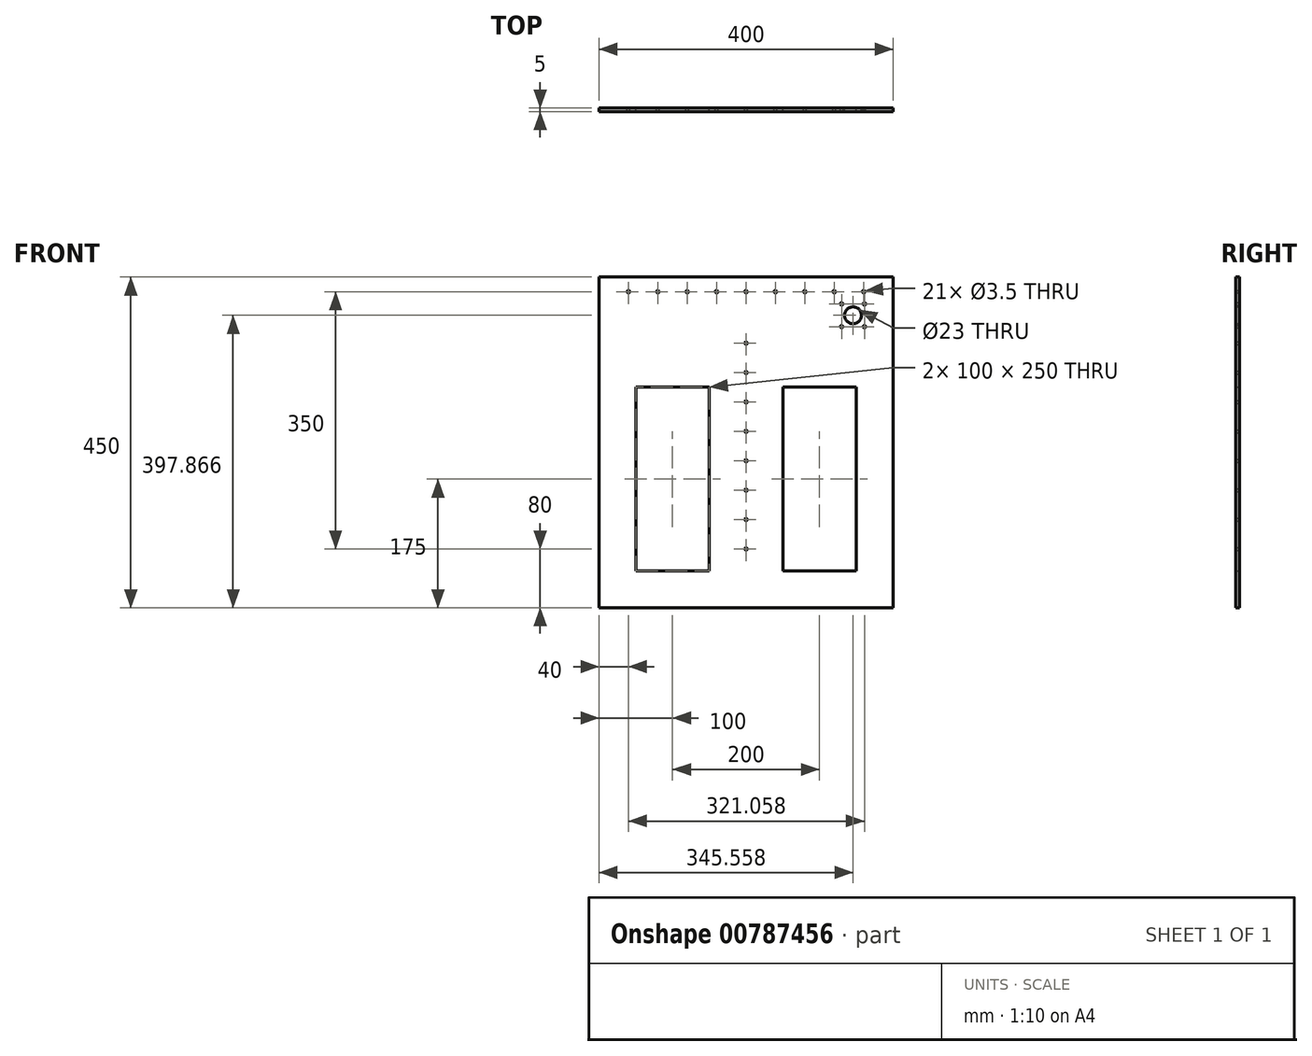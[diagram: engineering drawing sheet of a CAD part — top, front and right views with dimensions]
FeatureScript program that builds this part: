
annotation { "Feature Type Name" : "Feature", "Feature Type Description" : "" }
export const myFeature = defineFeature(function(context is Context, id is Id, definition is map)
    precondition{}
    {
        {
            var Q0;
            Q0=qCreatedBy(makeId("Front.planeOp"),FACE);
            var sketch = newSketch(context, id + "F0", { "sketchPlane" : qUnion([Q0])});
            skLineSegment(sketch, "E0.bottom", {"start": v(0, 0) * mm, "end": v(400, 0) * mm});
            skLineSegment(sketch, "E0.top", {"start": v(0, 450) * mm, "end": v(400, 450) * mm});
            skLineSegment(sketch, "E0.left", {"start": v(0, 0) * mm, "end": v(0, 450) * mm});
            skLineSegment(sketch, "E0.right", {"start": v(400, 0) * mm, "end": v(400, 450) * mm});
            skLineSegment(sketch, "E1", {"start": v(200, 0) * mm, "end": v(200, 450) * mm, "construction": true});
            skLineSegment(sketch, "E2", {"start": v(20.39, 430) * mm, "end": v(471, 430) * mm, "construction": true});
            skCircle(sketch, "E3", {"center": v(40, 430) * mm, "radius": 1.75 * mm});
            skCircle(sketch, "E4.1.0.0", {"center": v(80, 430) * mm, "radius": 1.75 * mm});
            skCircle(sketch, "E4.2.0.0", {"center": v(120, 430) * mm, "radius": 1.75 * mm});
            skCircle(sketch, "E4.3.0.0", {"center": v(160, 430) * mm, "radius": 1.75 * mm});
            skCircle(sketch, "E4.4.0.0", {"center": v(200, 430) * mm, "radius": 1.75 * mm});
            skCircle(sketch, "E4.5.0.0", {"center": v(240, 430) * mm, "radius": 1.75 * mm});
            skCircle(sketch, "E4.6.0.0", {"center": v(280, 430) * mm, "radius": 1.75 * mm});
            skCircle(sketch, "E4.7.0.0", {"center": v(320, 430) * mm, "radius": 1.75 * mm});
            skCircle(sketch, "E4.8.0.0", {"center": v(360, 430) * mm, "radius": 1.75 * mm});
            skLineSegment(sketch, "E4.direction1", {"start": v(40, 430) * mm, "end": v(80, 430) * mm, "construction": true});
            skLineSegment(sketch, "E5.bottom", {"start": v(50, 50) * mm, "end": v(150, 50) * mm});
            skLineSegment(sketch, "E5.top", {"start": v(50, 300) * mm, "end": v(150, 300) * mm});
            skLineSegment(sketch, "E5.left", {"start": v(50, 50) * mm, "end": v(50, 300) * mm});
            skLineSegment(sketch, "E5.right", {"start": v(150, 50) * mm, "end": v(150, 300) * mm});
            skLineSegment(sketch, "E6.MirrorCS", {"start": v(350, 300) * mm, "end": v(250, 300) * mm});
            skLineSegment(sketch, "E7.MirrorCS", {"start": v(250, 50) * mm, "end": v(250, 300) * mm});
            skLineSegment(sketch, "E8.MirrorCS", {"start": v(350, 50) * mm, "end": v(250, 50) * mm});
            skLineSegment(sketch, "E9.MirrorCS", {"start": v(350, 50) * mm, "end": v(350, 300) * mm});
            skLineSegment(sketch, "E10", {"start": v(200, -186.91) * mm, "end": v(200, 485.92) * mm, "construction": true});
            skCircle(sketch, "E11", {"center": v(200, 80) * mm, "radius": 1.75 * mm});
            skCircle(sketch, "E12.1.0.0", {"center": v(200, 120) * mm, "radius": 1.75 * mm});
            skCircle(sketch, "E12.2.0.0", {"center": v(200, 160) * mm, "radius": 1.75 * mm});
            skCircle(sketch, "E12.3.0.0", {"center": v(200, 200) * mm, "radius": 1.75 * mm});
            skCircle(sketch, "E12.4.0.0", {"center": v(200, 240) * mm, "radius": 1.75 * mm});
            skCircle(sketch, "E12.5.0.0", {"center": v(200, 280) * mm, "radius": 1.75 * mm});
            skCircle(sketch, "E12.6.0.0", {"center": v(200, 320) * mm, "radius": 1.75 * mm});
            skCircle(sketch, "E12.7.0.0", {"center": v(200, 360) * mm, "radius": 1.75 * mm});
            skLineSegment(sketch, "E12.direction1", {"start": v(200, 80) * mm, "end": v(200, 120) * mm, "construction": true});
            skLineSegment(sketch, "E13", {"start": v(345.56, 476.63) * mm, "end": v(345.56, 330.03) * mm, "construction": true});
            skLineSegment(sketch, "E14", {"start": v(268.91, 397.87) * mm, "end": v(425.85, 397.87) * mm, "construction": true});
            skCircle(sketch, "E15", {"center": v(345.56, 397.87) * mm, "radius": 11.5 * mm});
            skCircle(sketch, "E16", {"center": v(330.06, 413.37) * mm, "radius": 1.75 * mm});
            skCircle(sketch, "E17.MirrorC", {"center": v(361.06, 413.37) * mm, "radius": 1.75 * mm});
            skCircle(sketch, "E18.MirrorC", {"center": v(330.06, 382.37) * mm, "radius": 1.75 * mm});
            skCircle(sketch, "E19.MirrorC", {"center": v(361.06, 382.37) * mm, "radius": 1.75 * mm});
            skSolve(sketch);
        }
        {
            var Q0;
            Q0=makeQuery(id+"F0.imprint","IMPRINT",FACE,{"disambiguationData":[TD([[makeQuery(id+"F0.imprint","IMPRINT",EDGE,{"derivedFrom":sQuery(id+"F0.wireOp",EDGE,"E0.bottom")}),1.0]])]});
            extrude(context, id + "F1", {"entities" : qUnion([Q0]), "depth" : 5 * mm, "offsetDistance" : 25 * mm});
        }
    });
